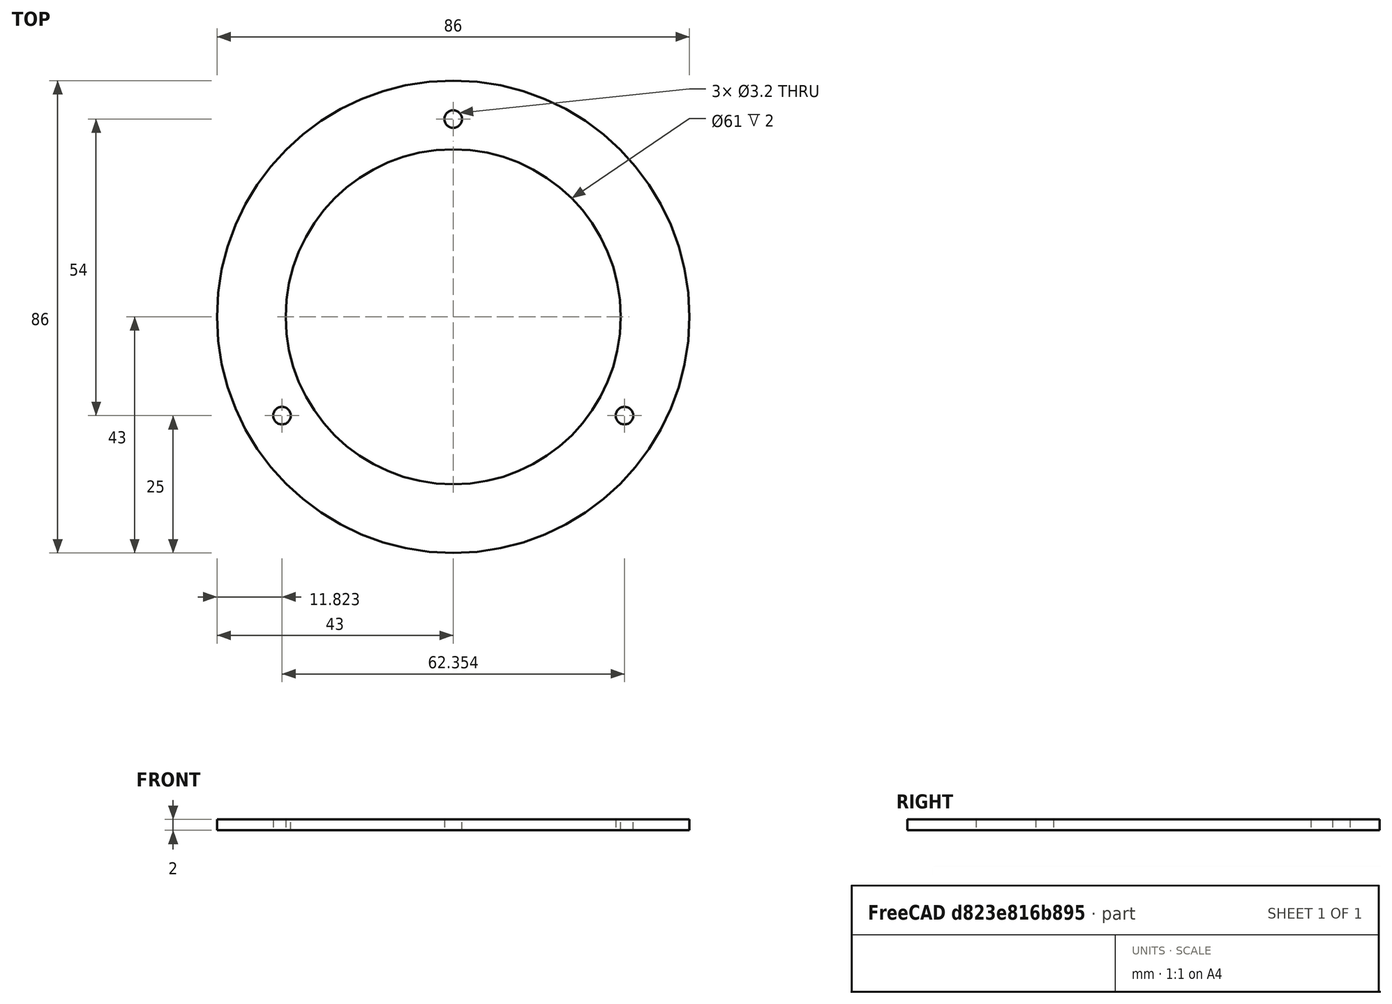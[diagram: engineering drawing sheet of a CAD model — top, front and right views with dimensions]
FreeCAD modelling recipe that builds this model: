
FCSTD DOCUMENT  (FreeCAD 0.19R24276 (Git))
Label: Ring_underglass_h_2_0mm_V3
License: All rights reserved
LicenseURL: http://en.wikipedia.org/wiki/All_rights_reserved
objects: Sketcher::SketchObject×1, PartDesign::Pad×1, PartDesign::Body×1
note: 4 computed .brp shape members not serialized (recipe doc carries the construction recipe); baked Part::Feature solids carry a one-line shape summary decoded from their .brp

FEATURE [Sketcher::SketchObject] Sketch006  label="Sketch006_d72_3_otv_d3.2"
  FullyConstrained = true
  MapMode = 5
  Placement = pos=(0,0,22) rot=(0,0,1;0rad)
  sketch-geometry (9):
    g0: LineSegment StartX=0 StartY=36 StartZ=0 EndX=-31.1769 EndY=-18 EndZ=0
    g1: LineSegment StartX=-31.1769 StartY=-18 StartZ=0 EndX=31.1769 EndY=-18 EndZ=0
    g2: LineSegment StartX=31.1769 StartY=-18 StartZ=0 EndX=0 EndY=36 EndZ=0
    g3: Circle CenterX=0 CenterY=0 CenterZ=0 NormalX=0 NormalY=0 NormalZ=1 AngleXU=0 Radius=36
    g4: Circle CenterX=0 CenterY=36 CenterZ=0 NormalX=0 NormalY=0 NormalZ=1 AngleXU=0 Radius=1.6
    g5: Circle CenterX=31.1769 CenterY=-18 CenterZ=0 NormalX=0 NormalY=0 NormalZ=1 AngleXU=0 Radius=1.6
    g6: Circle CenterX=-31.1769 CenterY=-18 CenterZ=0 NormalX=0 NormalY=0 NormalZ=1 AngleXU=0 Radius=1.6
    g7: Circle CenterX=0 CenterY=0 CenterZ=0 NormalX=0 NormalY=0 NormalZ=1 AngleXU=0 Radius=43
    g8: Circle CenterX=0 CenterY=0 CenterZ=0 NormalX=0 NormalY=0 NormalZ=1 AngleXU=0 Radius=30.5
  constraints (21):
    c: Coincident(g0,g1)
    c: Coincident(g1,g2)
    c: Coincident(g2,g0)
    c: Equal(g0,g1)
    c: Equal(g0,g2)
    c: PointOnObject(g0,g3)
    c: PointOnObject(g1,g3)
    c: PointOnObject(g2,g3)
    c: Coincident(g3,g-1)
    c: PointOnObject(g2,g-2)
    c: Diameter(g3) = 72
    c: Coincident(g4,g0)
    c: Coincident(g5,g1)
    c: Coincident(g6,g0)
    c: Diameter(g6) = 3.2
    c: Equal(g6,g4)
    c: Equal(g6,g5)
    c: Coincident(g7,g-1)
    c: Diameter(g7) = 86
    c: Coincident(g8,g7)
    c: Diameter(g8) = 61
FEATURE [PartDesign::Pad] Pad  label="Pad_h2"
  Direction = (1,1,1)
  Length = 2
  Length2 = 100
  Placement = pos=(0,0,22) rot=(0,0,1;0rad)
  Profile = -> Sketch006
  Type = 0
FEATURE [PartDesign::Body] Body
  Group = -> [Sketch006,Pad]
  Origin = -> Origin
  Tip = -> Pad
